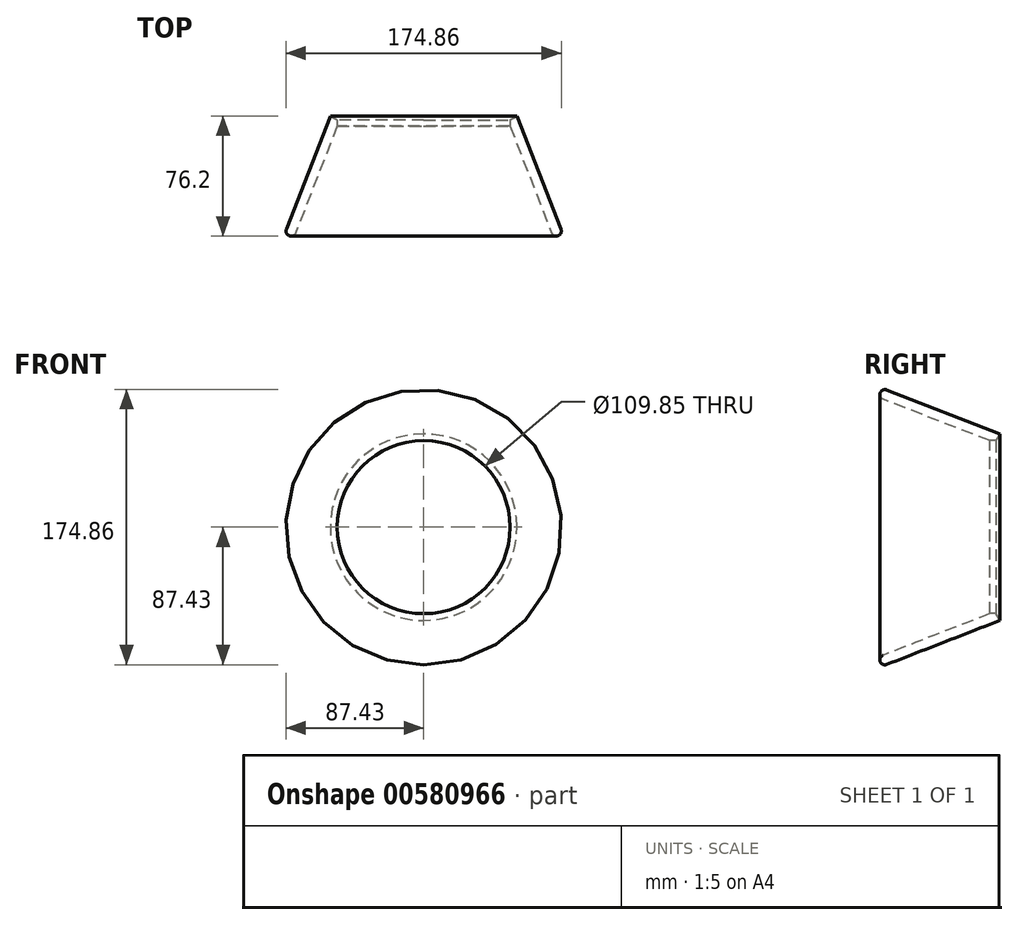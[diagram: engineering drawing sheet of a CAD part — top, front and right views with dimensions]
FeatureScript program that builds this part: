
annotation { "Feature Type Name" : "Feature", "Feature Type Description" : "" }
export const myFeature = defineFeature(function(context is Context, id is Id, definition is map)
    precondition{}
    {
        {
            var Q0;
            Q0=qCreatedBy(makeId("Front.planeOp"),FACE);
            var sketch = newSketch(context, id + "F0", { "sketchPlane" : qUnion([Q0])});
            skCircle(sketch, "E0", {"center": v(0, 0) * mm, "radius": 59.27 * mm});
            skSolve(sketch);
        }
        {
            var Q0;
            Q0=qCreatedBy(makeId("Front.planeOp"),FACE);
            cPlane(context, id + "F1", {"entities" : qUnion([Q0]), "cplaneType" : CPlaneType.OFFSET, "offset" : 76.2 * mm, "width" : 152.4 * mm, "height" : 152.4 * mm});
        }
        {
            var Q0;
            Q0=qCreatedBy(id+"F1.planeOp",FACE);
            var sketch = newSketch(context, id + "F2", { "sketchPlane" : qUnion([Q0])});
            skCircle(sketch, "E1", {"center": v(0, 0) * mm, "radius": 88.9 * mm});
            skSolve(sketch);
        }
        {
            var Q0;
            Q0=makeQuery(id+"F2.imprint","IMPRINT",FACE,{"disambiguationData":[TD([[makeQuery(id+"F2.imprint","IMPRINT",EDGE,{"derivedFrom":sQuery(id+"F2.wireOp",EDGE,"E1")}),1.0]])]});
            var Q1;
            Q1=makeQuery(id+"F0.imprint","IMPRINT",FACE,{"disambiguationData":[TD([[makeQuery(id+"F0.imprint","IMPRINT",EDGE,{"derivedFrom":sQuery(id+"F0.wireOp",EDGE,"E0")}),1.0]])]});
            loft(context, id + "F3", {"sheetProfilesArray" : [{ "sheetProfileEntities" : qUnion([Q0]) }, { "sheetProfileEntities" : qUnion([Q1]) }]});
        }
        {
            var Q0;
            Q0=makeQuery(id+"F3.opLoft","CAP_FACE",FACE,{"disambiguationData":[OSD([makeQuery(id+"F2.imprint","IMPRINT",FACE,{"disambiguationData":[TD([[makeQuery(id+"F2.imprint","IMPRINT",EDGE,{"derivedFrom":sQuery(id+"F2.wireOp",EDGE,"E1")}),1.0]])]})])],"isStart":true});
            shell(context, id + "F4", {"entities" : qUnion([Q0]), "thickness" : 6.35 * mm});
        }
        {
            var Q0;
            Q0=makeQuery(id+"F4.opShell","OFFSET_FACE",FACE,{"disambiguationData":[OSD([makeQuery(id+"F0.imprint","IMPRINT",FACE,{"disambiguationData":[TD([[makeQuery(id+"F0.imprint","IMPRINT",EDGE,{"derivedFrom":sQuery(id+"F0.wireOp",EDGE,"E0")}),1.0]])]})])]});
            var sketch = newSketch(context, id + "F5", { "sketchPlane" : qUnion([Q0])});
            skCircle(sketch, "E2", {"center": v(0, 0) * mm, "radius": 54.92 * mm});
            skSolve(sketch);
        }
        {
            var Q0;
            Q0 = qSketchRegion(id + "F5", true);
            extrude(context, id + "F6", {"entities" : qUnion([Q0]), "operationType" : NewBodyOperationType.REMOVE, "endBound" : BoundingType.THROUGH_ALL, "oppositeDirection" : true, "depth" : 25.4 * mm, "offsetDistance" : 25.4 * mm});
        }
        {
            var Q0;
            Q0=makeQuery(id+"F3.opLoft","CAP_FACE",FACE,{"disambiguationData":[OSD([makeQuery(id+"F2.imprint","IMPRINT",FACE,{"disambiguationData":[TD([[makeQuery(id+"F2.imprint","IMPRINT",EDGE,{"derivedFrom":sQuery(id+"F2.wireOp",EDGE,"E1")}),1.0]])]})])],"isStart":true});
            fillet(context, id + "F7", {"entities" : qUnion([Q0]), "radius" : 3.17 * mm, "tangentPropagation" : true, "allowEdgeOverflow" : false});
        }
        {
            var Q0;
            Q0=qCreatedBy(makeId("Top.planeOp"),FACE);
            var sketch = newSketch(context, id + "F8", { "sketchPlane" : qUnion([Q0])});
            skArc(sketch, "E3", {"start": v(-59.27, 0) * mm, "mid": v(-30.77, -12.35) * mm, "end": v(0, -16.57) * mm});
            skLineSegment(sketch, "E4", {"start": v(0, 0) * mm, "end": v(-59.27, 0) * mm});
            skLineSegment(sketch, "E5", {"start": v(0, 0) * mm, "end": v(0, -16.57) * mm});
            skSolve(sketch);
        }
        {
            var Q0;
            Q0 = qSketchRegion(id + "F8", true);
            var Q1;
            Q1=sQuery(id+"F8.wireOp",EDGE,"E5");
            revolve(context, id + "F9", {"operationType" : NewBodyOperationType.REMOVE, "entities" : qUnion([Q0]), "axis" : qUnion([Q1]), "revolveType" : RevolveType.FULL, "oppositeDirection" : true});
        }
    });
